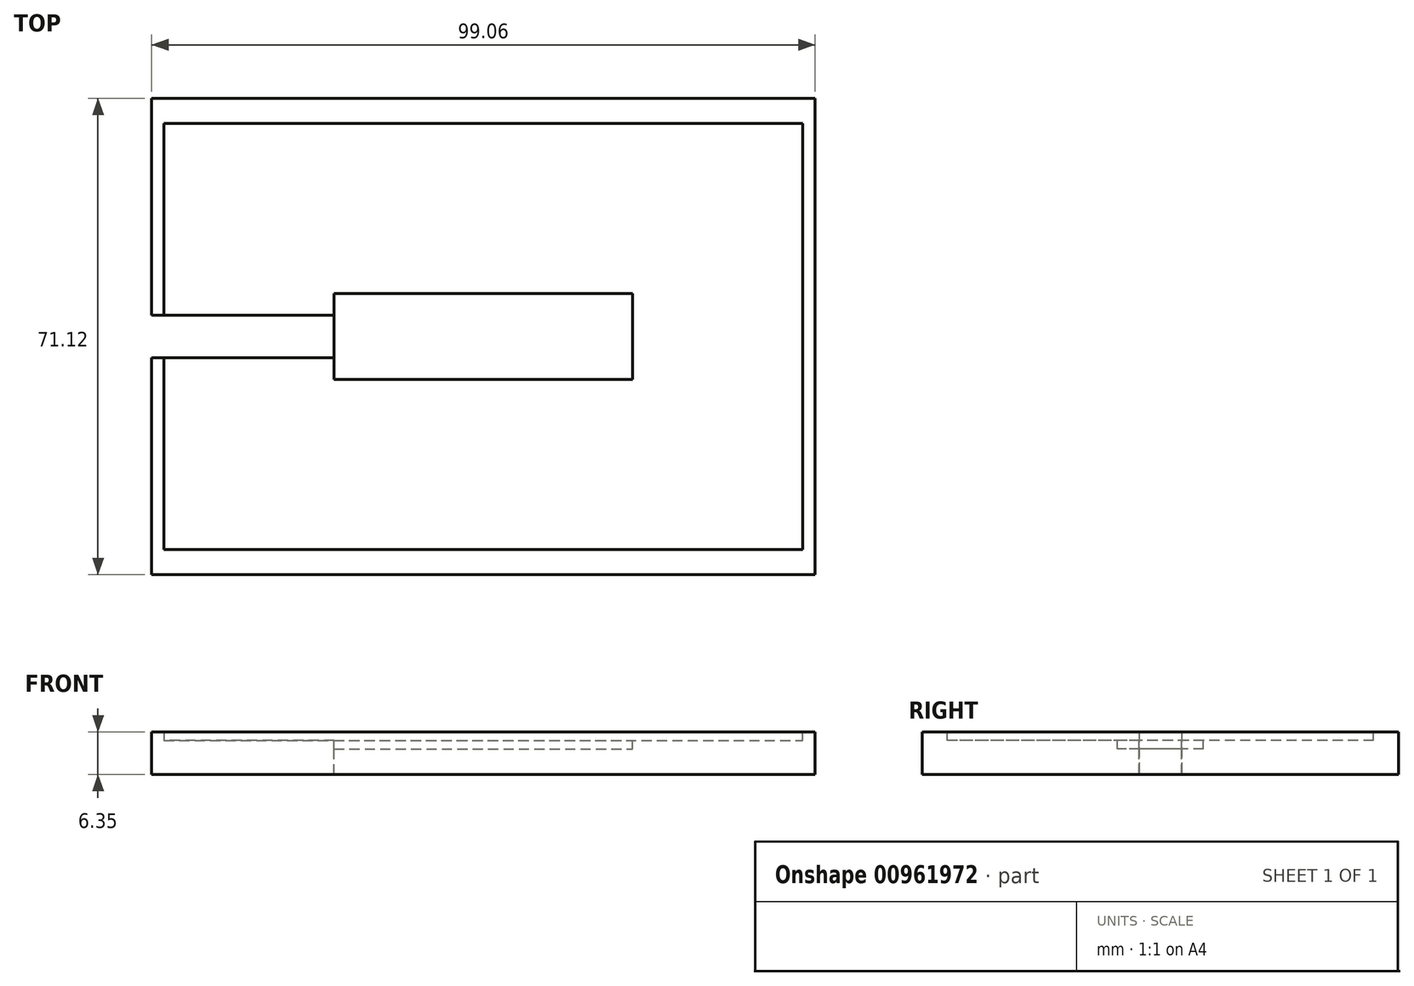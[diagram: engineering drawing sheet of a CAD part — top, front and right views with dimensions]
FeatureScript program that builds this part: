
annotation { "Feature Type Name" : "Feature", "Feature Type Description" : "" }
export const myFeature = defineFeature(function(context is Context, id is Id, definition is map)
    precondition{}
    {
        {
            var Q0;
            Q0=qCreatedBy(makeId("Top.planeOp"),FACE);
            var sketch = newSketch(context, id + "F0", { "sketchPlane" : qUnion([Q0])});
            skLineSegment(sketch, "E0.bottom", {"start": v(-49.53, 35.56) * mm, "end": v(49.53, 35.56) * mm});
            skLineSegment(sketch, "E0.top", {"start": v(-49.53, -35.56) * mm, "end": v(49.53, -35.56) * mm});
            skLineSegment(sketch, "E0.left", {"start": v(-49.53, 35.56) * mm, "end": v(-49.53, -35.56) * mm});
            skLineSegment(sketch, "E0.right", {"start": v(49.53, 35.56) * mm, "end": v(49.53, -35.56) * mm});
            skPoint(sketch, "E0.middle", {"position": v(0, 0) * mm});
            skSolve(sketch);
        }
        {
            var Q0;
            Q0 = qSketchRegion(id + "F0", true);
            extrude(context, id + "F1", {"entities" : qUnion([Q0]), "depth" : 6.35 * mm, "offsetDistance" : 25.4 * mm});
        }
        {
            var Q0;
            Q0=makeQuery(id+"F1.opExtrude","CAP_FACE",FACE,{"disambiguationData":[OSD([sQuery(id+"F0.wireOp",EDGE,"E0.bottom"),sQuery(id+"F0.wireOp",EDGE,"E0.top"),sQuery(id+"F0.wireOp",EDGE,"E0.left"),sQuery(id+"F0.wireOp",EDGE,"E0.right")])],"isStart":false});
            var sketch = newSketch(context, id + "F2", { "sketchPlane" : qUnion([Q0])});
            skLineSegment(sketch, "E1.bottom", {"start": v(-47.69, 31.81) * mm, "end": v(47.69, 31.81) * mm});
            skLineSegment(sketch, "E1.top", {"start": v(-47.69, -31.81) * mm, "end": v(47.69, -31.81) * mm});
            skLineSegment(sketch, "E1.left", {"start": v(-47.69, 31.81) * mm, "end": v(-47.69, -31.81) * mm});
            skLineSegment(sketch, "E1.right", {"start": v(47.69, 31.81) * mm, "end": v(47.69, -31.81) * mm});
            skPoint(sketch, "E1.middle", {"position": v(0, 0) * mm});
            skSolve(sketch);
        }
        {
            var Q0;
            Q0 = qSketchRegion(id + "F2", true);
            extrude(context, id + "F3", {"entities" : qUnion([Q0]), "operationType" : NewBodyOperationType.REMOVE, "oppositeDirection" : true, "depth" : 1.27 * mm, "offsetDistance" : 25.4 * mm});
        }
        {
            var Q0;
            Q0=makeQuery(id+"F3.boolean.opBoolean","COPY",FACE,{"derivedFrom":makeQuery(id+"F3.opExtrude","CAP_FACE",FACE,{"disambiguationData":[OSD([sQuery(id+"F2.wireOp",EDGE,"E1.bottom"),sQuery(id+"F2.wireOp",EDGE,"E1.top"),sQuery(id+"F2.wireOp",EDGE,"E1.left"),sQuery(id+"F2.wireOp",EDGE,"E1.right")])],"isStart":false})});
            var sketch = newSketch(context, id + "F4", { "sketchPlane" : qUnion([Q0])});
            skLineSegment(sketch, "E2.bottom", {"start": v(-22.29, 6.41) * mm, "end": v(22.29, 6.41) * mm});
            skLineSegment(sketch, "E2.top", {"start": v(-22.29, -6.41) * mm, "end": v(22.29, -6.41) * mm});
            skLineSegment(sketch, "E2.left", {"start": v(-22.29, 6.41) * mm, "end": v(-22.29, -6.41) * mm});
            skLineSegment(sketch, "E2.right", {"start": v(22.29, 6.41) * mm, "end": v(22.29, -6.41) * mm});
            skPoint(sketch, "E2.middle", {"position": v(0, 0) * mm});
            skSolve(sketch);
        }
        {
            var Q0;
            Q0 = qSketchRegion(id + "F4", true);
            extrude(context, id + "F5", {"entities" : qUnion([Q0]), "operationType" : NewBodyOperationType.REMOVE, "oppositeDirection" : true, "depth" : 1.27 * mm, "offsetDistance" : 25.4 * mm});
        }
        {
            var Q0;
            Q0=makeQuery(id+"F1.opExtrude","SWEPT_FACE",FACE,{"disambiguationData":[OSD([sQuery(id+"F0.wireOp",EDGE,"E0.left")])]});
            var sketch = newSketch(context, id + "F6", { "sketchPlane" : qUnion([Q0])});
            skLineSegment(sketch, "E3.bottom", {"start": v(-3.18, 6.35) * mm, "end": v(3.18, 6.35) * mm});
            skLineSegment(sketch, "E3.top", {"start": v(-3.18, 0) * mm, "end": v(3.18, 0) * mm});
            skLineSegment(sketch, "E3.left", {"start": v(-3.18, 6.35) * mm, "end": v(-3.18, 0) * mm});
            skLineSegment(sketch, "E3.right", {"start": v(3.18, 6.35) * mm, "end": v(3.18, 0) * mm});
            skPoint(sketch, "E3.middle", {"position": v(0, 3.18) * mm});
            skSolve(sketch);
        }
        {
            var Q0;
            Q0 = qSketchRegion(id + "F6", true);
            var Q1;
            Q1=makeQuery(id+"F5.boolean.opBoolean","COPY",FACE,{"derivedFrom":makeQuery(id+"F5.opExtrude","SWEPT_FACE",FACE,{"disambiguationData":[OSD([sQuery(id+"F4.wireOp",EDGE,"E2.left")])]})});
            extrude(context, id + "F7", {"entities" : qUnion([Q0]), "operationType" : NewBodyOperationType.REMOVE, "endBound" : BoundingType.UP_TO_SURFACE, "oppositeDirection" : true, "depth" : 25.4 * mm, "endBoundEntityFace" : qUnion([Q1]), "offsetDistance" : 25.4 * mm});
        }
    });
